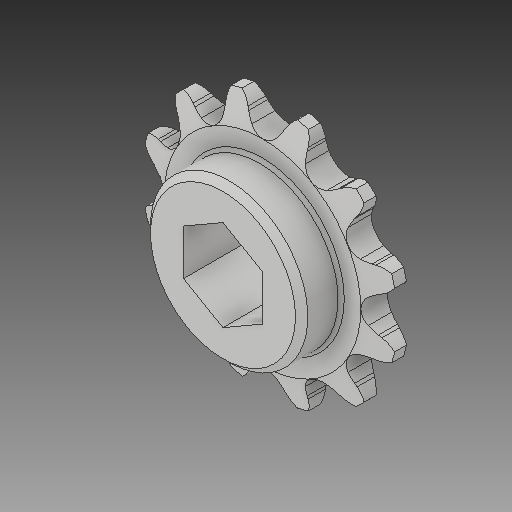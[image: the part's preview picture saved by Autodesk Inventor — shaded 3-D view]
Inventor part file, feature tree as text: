
AUTODESK INVENTOR PART (.ipt)
format: ipt  version: 2017 (Build 210142000, 142)  size: 379,904 bytes
history: native  units: in
note: dims shown in document units (in); Inventor stores cm internally (conversion verified against a paired STEP export)
features: chamfer x1
ambient origin geometry x8: Origin, YZ Plane, XZ Plane, XY Plane, X Axis, Y Axis, Z Axis, Center Point
bodies: Solid1 (feature_tree)
feature tree (1):
  chamfer  "Chamfer1"  [1 undecoded]
note: 1 required parameter value undecoded (feature->parameter linkage not recoverable at this tier; creation-order binding heuristic only, values carry confidence <= 0.55)
